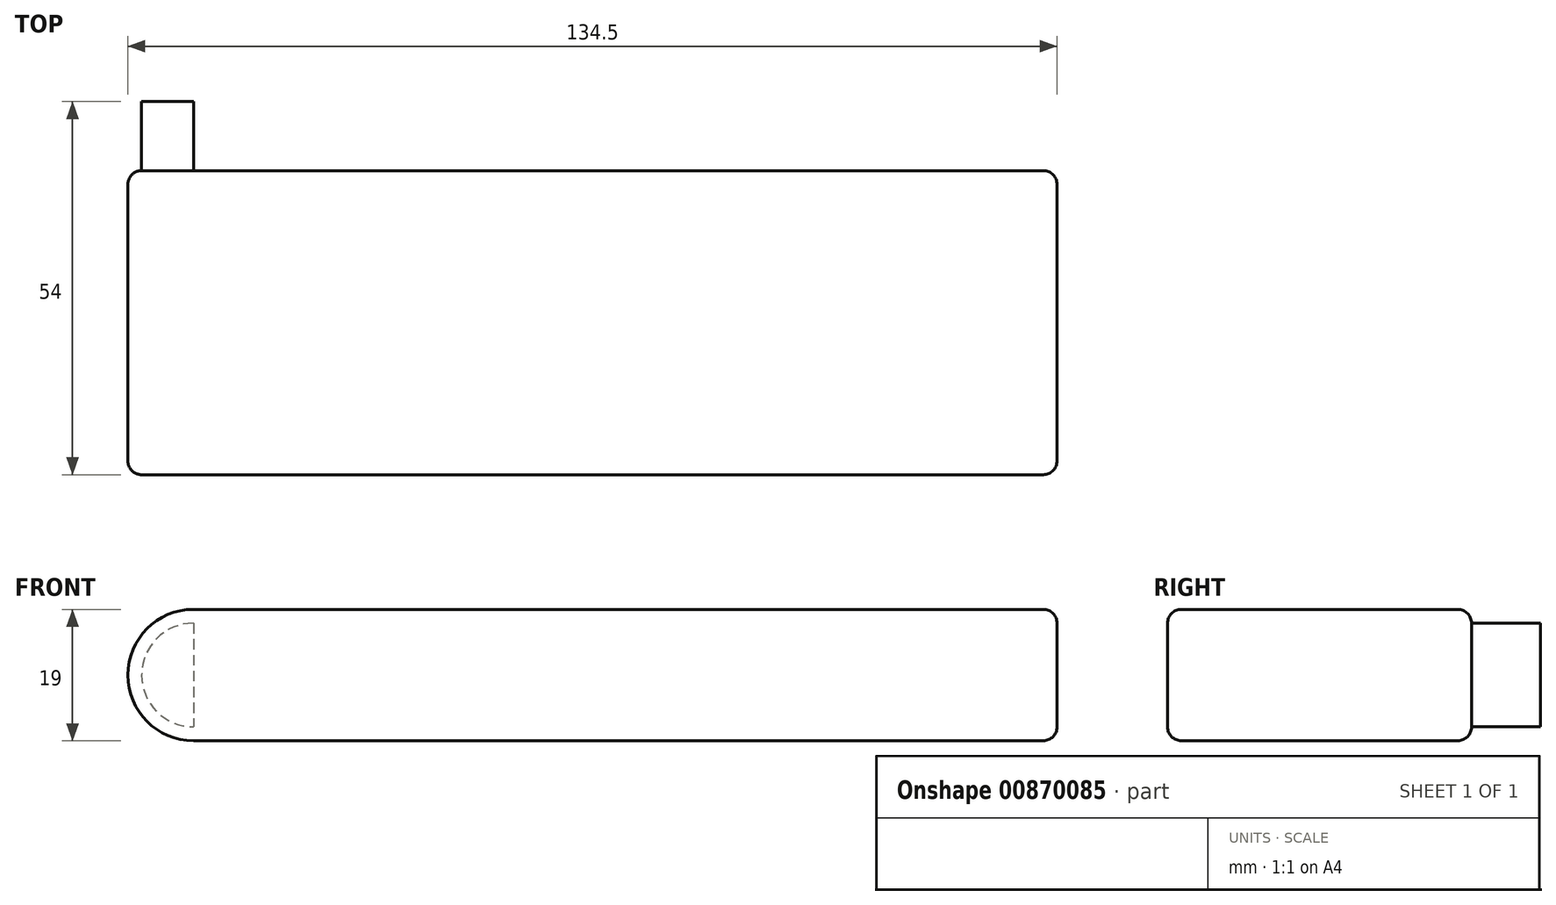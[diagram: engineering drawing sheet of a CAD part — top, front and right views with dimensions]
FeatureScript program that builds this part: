
annotation { "Feature Type Name" : "Feature", "Feature Type Description" : "" }
export const myFeature = defineFeature(function(context is Context, id is Id, definition is map)
    precondition{}
    {
        {
            var Q0;
            Q0=qCreatedBy(makeId("Front.planeOp"),FACE);
            var sketch = newSketch(context, id + "F0", { "sketchPlane" : qUnion([Q0])});
            skCircle(sketch, "E0", {"center": v(-68.72, 0) * mm, "radius": 9.5 * mm});
            skLineSegment(sketch, "E1", {"start": v(-68.72, 9.5) * mm, "end": v(56.28, 9.5) * mm});
            skLineSegment(sketch, "E2", {"start": v(-68.72, -9.5) * mm, "end": v(56.28, -9.5) * mm});
            skLineSegment(sketch, "E3", {"start": v(56.28, -9.5) * mm, "end": v(56.28, 9.5) * mm});
            skSolve(sketch);
        }
        {
            var Q0;
            {var subQ0=sQuery(id+"F0.wireOp",EDGE,"E0");var subQ1=makeQuery(id+"F0.imprint","INTERSECT",VERTEX,{"derivedFrom":[subQ0,sQuery(id+"F0.wireOp",EDGE,"E1")]});Q0=makeQuery(id+"F0.imprint","IMPRINT",FACE,{"disambiguationData":[TD([[makeQuery(id+"F0.imprint","IMPRINT",EDGE,{"disambiguationData":[TD([[subQ1,-1.0]])],"derivedFrom":subQ0}),1.0]])]});}
            var Q1;
            {var subQ0=sQuery(id+"F0.wireOp",EDGE,"E1");Q1=makeQuery(id+"F0.imprint","IMPRINT",FACE,{"disambiguationData":[TD([[makeQuery(id+"F0.imprint","IMPRINT",EDGE,{"derivedFrom":subQ0}),-1.0]])]});}
            extrude(context, id + "F1", {"entities" : qUnion([Q0, Q1]), "depth" : 44 * mm, "offsetDistance" : 25 * mm});
        }
        {
            var Q0;
            Q0=makeQuery(id+"F1.opExtrude","CAP_EDGE",EDGE,{"disambiguationData":[OSD([sQuery(id+"F0.wireOp",EDGE,"E1")])],"isStart":false});
            var Q1;
            Q1=makeQuery(id+"F1.opExtrude","SWEPT_EDGE",EDGE,{"disambiguationData":[OSD([sQuery(id+"F0.wireOp",EDGE,"E1"),sQuery(id+"F0.wireOp",EDGE,"E3")])]});
            var Q2;
            Q2=makeQuery(id+"F1.opExtrude","SWEPT_EDGE",EDGE,{"disambiguationData":[OSD([sQuery(id+"F0.wireOp",EDGE,"E2"),sQuery(id+"F0.wireOp",EDGE,"E3")])]});
            var Q3;
            Q3=makeQuery(id+"F1.opExtrude","CAP_EDGE",EDGE,{"disambiguationData":[OSD([sQuery(id+"F0.wireOp",EDGE,"E3")])],"isStart":false});
            var Q4;
            Q4=makeQuery(id+"F1.opExtrude","CAP_EDGE",EDGE,{"disambiguationData":[OSD([sQuery(id+"F0.wireOp",EDGE,"E3")])],"isStart":true});
            var Q5;
            Q5=makeQuery(id+"F1.opExtrude","CAP_EDGE",EDGE,{"disambiguationData":[OSD([sQuery(id+"F0.wireOp",EDGE,"E2")])],"isStart":true});
            var Q6;
            Q6=makeQuery(id+"F1.opExtrude","CAP_EDGE",EDGE,{"disambiguationData":[OSD([sQuery(id+"F0.wireOp",EDGE,"E1")])],"isStart":true});
            fillet(context, id + "F2", {"entities" : qUnion([Q0, Q1, Q2, Q3, Q4, Q5, Q6]), "radius" : 2 * mm, "tangentPropagation" : true, "allowEdgeOverflow" : false});
        }
        {
            var Q0;
            Q0=makeQuery(id+"F1.opExtrude","CAP_FACE",FACE,{"disambiguationData":[OSD([sQuery(id+"F0.wireOp",EDGE,"E0"),sQuery(id+"F0.wireOp",EDGE,"E1"),sQuery(id+"F0.wireOp",EDGE,"E2"),sQuery(id+"F0.wireOp",EDGE,"E3")])],"isStart":true});
            var sketch = newSketch(context, id + "F3", { "sketchPlane" : qUnion([Q0])});
            skLineSegment(sketch, "E4", {"start": v(68.72, 7.5) * mm, "end": v(68.72, -7.5) * mm});
            skSolve(sketch);
        }
        {
            var Q0;
            Q0=makeQuery(id+"F3.imprint","IMPRINT",FACE,{"disambiguationData":[TD([[makeQuery(id+"F3.imprint","IMPRINT",EDGE,{"derivedFrom":sQuery(id+"F3.wireOp",EDGE,"E4")}),1.0]])]});
            extrude(context, id + "F4", {"entities" : qUnion([Q0]), "operationType" : NewBodyOperationType.ADD, "depth" : 10 * mm, "offsetDistance" : 25 * mm});
        }
    });
